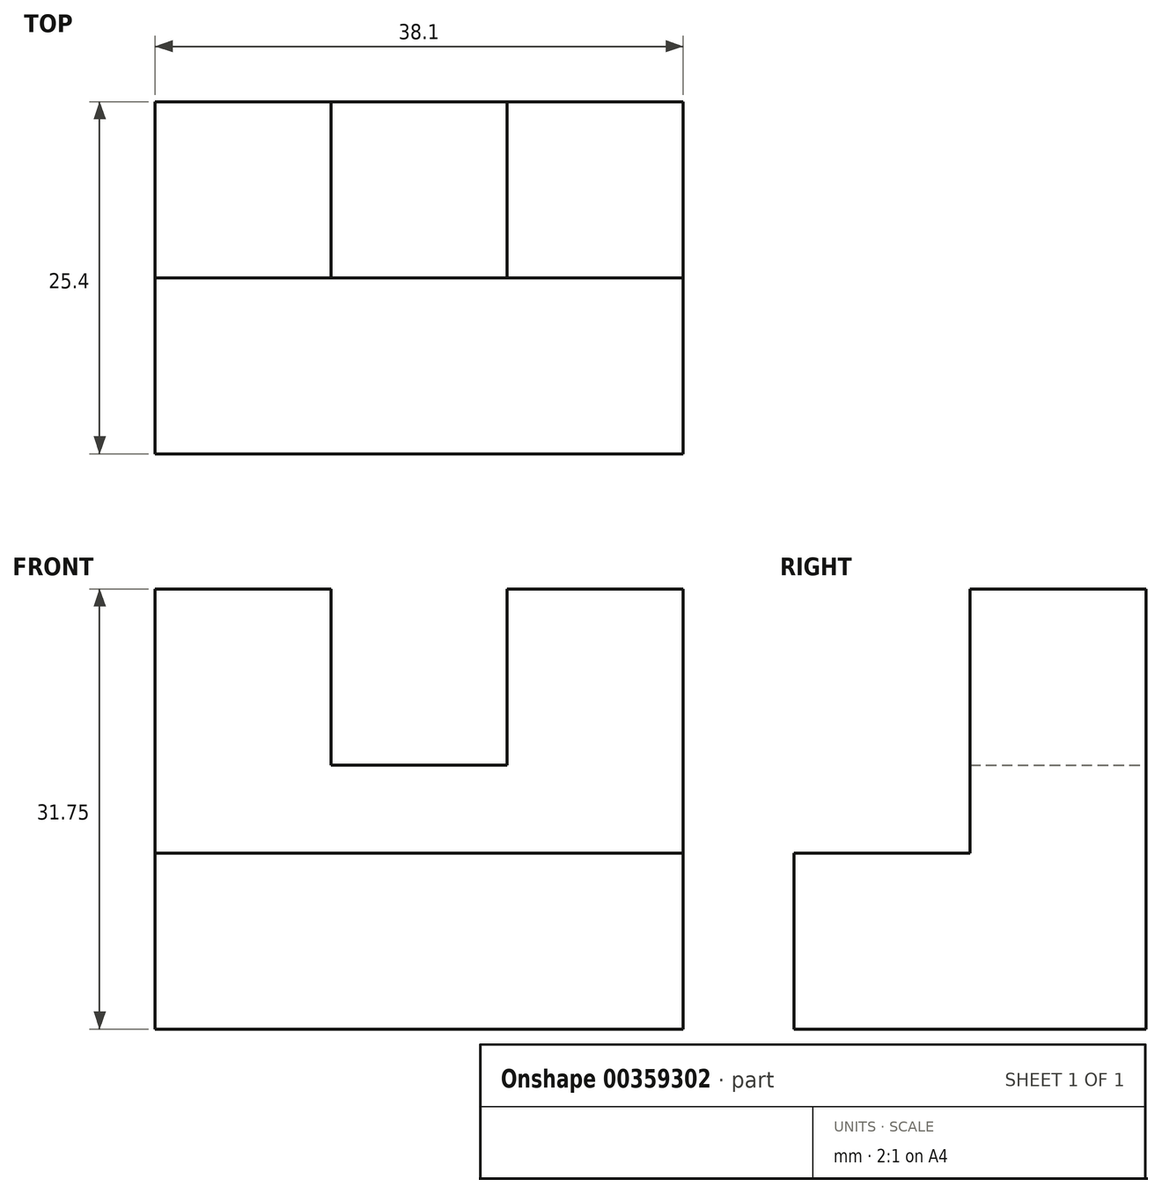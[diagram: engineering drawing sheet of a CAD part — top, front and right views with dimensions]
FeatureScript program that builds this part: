
annotation { "Feature Type Name" : "Feature", "Feature Type Description" : "" }
export const myFeature = defineFeature(function(context is Context, id is Id, definition is map)
    precondition{}
    {
        {
            var Q0;
            Q0=qCreatedBy(makeId("Front.planeOp"),FACE);
            var sketch = newSketch(context, id + "F0", { "sketchPlane" : qUnion([Q0])});
            skLineSegment(sketch, "E0", {"start": v(0, 0) * mm, "end": v(38.1, 0) * mm});
            skLineSegment(sketch, "E1", {"start": v(38.1, 0) * mm, "end": v(38.1, 31.75) * mm});
            skLineSegment(sketch, "E2", {"start": v(38.1, 31.75) * mm, "end": v(25.4, 31.75) * mm});
            skLineSegment(sketch, "E3", {"start": v(25.4, 31.75) * mm, "end": v(25.4, 19.05) * mm});
            skLineSegment(sketch, "E4", {"start": v(25.4, 19.05) * mm, "end": v(12.7, 19.05) * mm});
            skLineSegment(sketch, "E5", {"start": v(12.7, 19.05) * mm, "end": v(12.7, 31.75) * mm});
            skLineSegment(sketch, "E6", {"start": v(12.7, 31.75) * mm, "end": v(0, 31.75) * mm});
            skLineSegment(sketch, "E7", {"start": v(0, 31.75) * mm, "end": v(0, 0) * mm});
            skSolve(sketch);
        }
        {
            var Q0;
            Q0 = qSketchRegion(id + "F0", true);
            extrude(context, id + "F1", {"entities" : qUnion([Q0]), "depth" : 25.4 * mm});
        }
        {
            var Q0;
            Q0=makeQuery(id+"F1.opExtrude","CAP_FACE",FACE,{"disambiguationData":[OSD([sQuery(id+"F0.wireOp",EDGE,"E0"),sQuery(id+"F0.wireOp",EDGE,"E1"),sQuery(id+"F0.wireOp",EDGE,"E2"),sQuery(id+"F0.wireOp",EDGE,"E3"),sQuery(id+"F0.wireOp",EDGE,"E4"),sQuery(id+"F0.wireOp",EDGE,"E5"),sQuery(id+"F0.wireOp",EDGE,"E6"),sQuery(id+"F0.wireOp",EDGE,"E7")])],"isStart":false});
            var sketch = newSketch(context, id + "F2", { "sketchPlane" : qUnion([Q0])});
            skLineSegment(sketch, "E8", {"start": v(0, 12.7) * mm, "end": v(38.1, 12.7) * mm});
            skSolve(sketch);
        }
        {
            var Q0;
            {var subQ1=sQuery(id+"F2.wireOp",EDGE,"E8");Q0=makeQuery(id+"F2.imprint","IMPRINT",FACE,{"disambiguationData":[TD([[makeQuery(id+"F2.imprint","IMPRINT",EDGE,{"derivedFrom":subQ1}),1.0]])]});}
            extrude(context, id + "F3", {"entities" : qUnion([Q0]), "operationType" : NewBodyOperationType.REMOVE, "oppositeDirection" : true, "depth" : 12.7 * mm});
        }
    });
